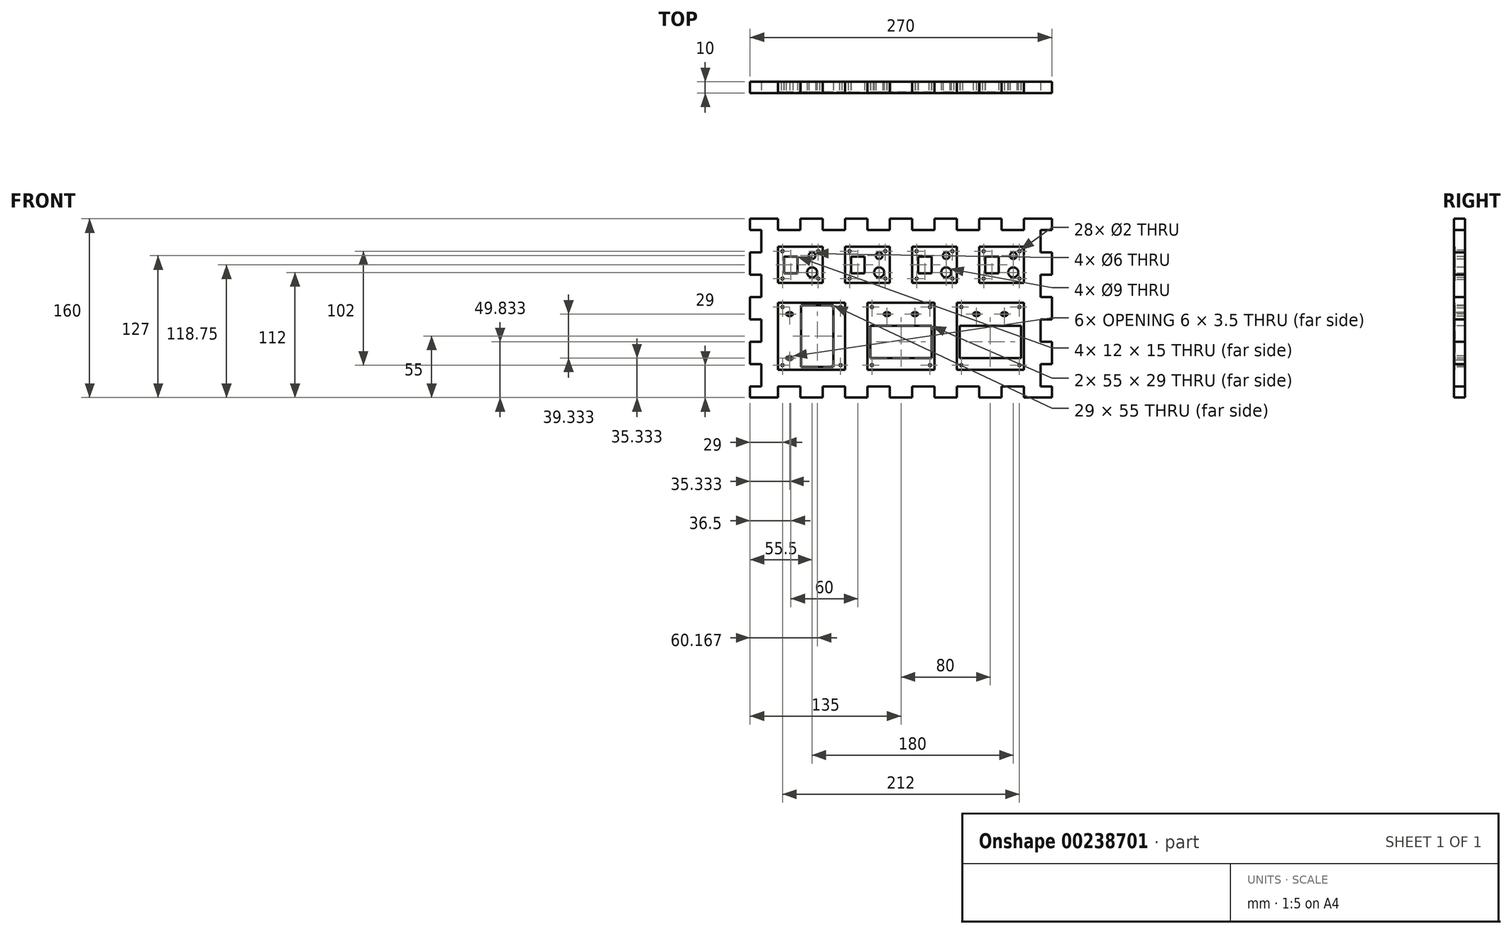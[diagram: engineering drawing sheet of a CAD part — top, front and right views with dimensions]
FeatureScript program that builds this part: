
annotation { "Feature Type Name" : "Feature", "Feature Type Description" : "" }
export const myFeature = defineFeature(function(context is Context, id is Id, definition is map)
    precondition{}
    {
        {
            var Q0;
            Q0=qCreatedBy(makeId("Front.planeOp"),FACE);
            var sketch = newSketch(context, id + "F0", { "sketchPlane" : qUnion([Q0])});
            skCircle(sketch, "E0", {"center": v(26.5, 16.25) * mm, "radius": 6.5 * mm, "construction": true});
            skCircle(sketch, "E1", {"center": v(45.5, 9.5) * mm, "radius": 4.5 * mm});
            skCircle(sketch, "E2", {"center": v(45.5, 9.5) * mm, "radius": 3 * mm});
            skCircle(sketch, "E3", {"center": v(45.5, 24.5) * mm, "radius": 3 * mm});
            skCircle(sketch, "E4", {"center": v(45.5, 24.5) * mm, "radius": 2.5 * mm});
            skLineSegment(sketch, "E5", {"start": v(45.5, 27.5) * mm, "end": v(45.5, 5) * mm, "construction": true});
            skPoint(sketch, "E6.positionSnap0", {"position": v(45.5, 16.25) * mm});
            skLineSegment(sketch, "E7.bottom", {"start": v(15, 32.5) * mm, "end": v(55, 32.5) * mm});
            skLineSegment(sketch, "E7.top", {"start": v(15, 0) * mm, "end": v(55, 0) * mm});
            skLineSegment(sketch, "E7.left", {"start": v(15, 32.5) * mm, "end": v(15, 0) * mm});
            skLineSegment(sketch, "E7.right", {"start": v(55, 32.5) * mm, "end": v(55, 0) * mm});
            skLineSegment(sketch, "E8", {"start": v(20.5, 22.25) * mm, "end": v(20.5, 23.75) * mm});
            skLineSegment(sketch, "E9", {"start": v(20.5, 23.75) * mm, "end": v(32.5, 23.75) * mm});
            skLineSegment(sketch, "E10", {"start": v(32.5, 23.75) * mm, "end": v(32.5, 22.25) * mm});
            skLineSegment(sketch, "E11", {"start": v(15, 16.25) * mm, "end": v(55, 16.25) * mm, "construction": true});
            skLineSegment(sketch, "E12.MirrorCS", {"start": v(32.5, 8.75) * mm, "end": v(32.5, 10.25) * mm});
            skLineSegment(sketch, "E13.MirrorCS", {"start": v(20.5, 8.75) * mm, "end": v(32.5, 8.75) * mm});
            skLineSegment(sketch, "E14.MirrorCS", {"start": v(20.5, 10.25) * mm, "end": v(20.5, 8.75) * mm});
            skLineSegment(sketch, "E15", {"start": v(50, 9.5) * mm, "end": v(55, 9.5) * mm, "construction": true});
            skLineSegment(sketch, "E16", {"start": v(41, 9.5) * mm, "end": v(41, 16.25) * mm, "construction": true});
            skLineSegment(sketch, "E17.bottom", {"start": v(32.5, 22.25) * mm, "end": v(20.5, 22.25) * mm});
            skLineSegment(sketch, "E17.top", {"start": v(32.5, 10.25) * mm, "end": v(20.5, 10.25) * mm});
            skLineSegment(sketch, "E17.left", {"start": v(32.5, 22.25) * mm, "end": v(32.5, 10.25) * mm});
            skLineSegment(sketch, "E17.right", {"start": v(20.5, 22.25) * mm, "end": v(20.5, 10.25) * mm});
            skLineSegment(sketch, "E18.bottom", {"start": v(24.5, 18.25) * mm, "end": v(28.5, 18.25) * mm});
            skLineSegment(sketch, "E18.top", {"start": v(24.5, 14.25) * mm, "end": v(28.5, 14.25) * mm});
            skLineSegment(sketch, "E18.left", {"start": v(24.5, 18.25) * mm, "end": v(24.5, 14.25) * mm});
            skLineSegment(sketch, "E18.right", {"start": v(28.5, 18.25) * mm, "end": v(28.5, 14.25) * mm});
            skLineSegment(sketch, "E19.1.0.0", {"start": v(92.5, 22.25) * mm, "end": v(80.5, 22.25) * mm});
            skCircle(sketch, "E19.1.0.1", {"center": v(105.5, 24.5) * mm, "radius": 2.5 * mm});
            skCircle(sketch, "E19.1.0.3", {"center": v(86.5, 16.25) * mm, "radius": 6.5 * mm, "construction": true});
            skLineSegment(sketch, "E19.1.0.4", {"start": v(115, 32.5) * mm, "end": v(115, 0) * mm});
            skLineSegment(sketch, "E19.1.0.5", {"start": v(75, 32.5) * mm, "end": v(115, 32.5) * mm});
            skLineSegment(sketch, "E19.1.0.6", {"start": v(84.5, 18.25) * mm, "end": v(84.5, 14.25) * mm});
            skLineSegment(sketch, "E19.1.0.7", {"start": v(84.5, 18.25) * mm, "end": v(88.5, 18.25) * mm});
            skLineSegment(sketch, "E19.1.0.8", {"start": v(92.5, 10.25) * mm, "end": v(80.5, 10.25) * mm});
            skLineSegment(sketch, "E19.1.0.9", {"start": v(80.5, 23.75) * mm, "end": v(92.5, 23.75) * mm});
            skCircle(sketch, "E19.1.0.10", {"center": v(105.5, 9.5) * mm, "radius": 4.5 * mm});
            skLineSegment(sketch, "E19.1.0.11", {"start": v(88.5, 18.25) * mm, "end": v(88.5, 14.25) * mm});
            skPoint(sketch, "E19.1.0.13", {"position": v(86.5, 16.25) * mm});
            skLineSegment(sketch, "E19.1.0.14", {"start": v(75, 32.5) * mm, "end": v(75, 0) * mm});
            skLineSegment(sketch, "E19.1.0.15", {"start": v(80.5, 8.75) * mm, "end": v(92.5, 8.75) * mm});
            skCircle(sketch, "E19.1.0.16", {"center": v(105.5, 9.5) * mm, "radius": 3 * mm});
            skCircle(sketch, "E19.1.0.17", {"center": v(105.5, 24.5) * mm, "radius": 3 * mm});
            skLineSegment(sketch, "E19.1.0.18", {"start": v(80.5, 22.25) * mm, "end": v(80.5, 10.25) * mm});
            skLineSegment(sketch, "E19.1.0.19", {"start": v(92.5, 22.25) * mm, "end": v(92.5, 10.25) * mm});
            skLineSegment(sketch, "E19.1.0.20", {"start": v(75, 0) * mm, "end": v(115, 0) * mm});
            skLineSegment(sketch, "E19.1.0.22", {"start": v(84.5, 14.25) * mm, "end": v(88.5, 14.25) * mm});
            skPoint(sketch, "E19.1.0.23", {"position": v(86.5, 16.25) * mm});
            skLineSegment(sketch, "E19.1.0.24", {"start": v(92.5, 23.75) * mm, "end": v(92.5, 22.25) * mm});
            skLineSegment(sketch, "E19.1.0.25", {"start": v(80.5, 22.25) * mm, "end": v(80.5, 23.75) * mm});
            skLineSegment(sketch, "E19.1.0.26", {"start": v(80.5, 10.25) * mm, "end": v(80.5, 8.75) * mm});
            skLineSegment(sketch, "E19.1.0.27", {"start": v(92.5, 8.75) * mm, "end": v(92.5, 10.25) * mm});
            skLineSegment(sketch, "E19.2.0.0", {"start": v(152.5, 22.25) * mm, "end": v(140.5, 22.25) * mm});
            skCircle(sketch, "E19.2.0.1", {"center": v(165.5, 24.5) * mm, "radius": 2.5 * mm});
            skCircle(sketch, "E19.2.0.3", {"center": v(146.5, 16.25) * mm, "radius": 6.5 * mm, "construction": true});
            skLineSegment(sketch, "E19.2.0.4", {"start": v(175, 32.5) * mm, "end": v(175, 0) * mm});
            skLineSegment(sketch, "E19.2.0.5", {"start": v(135, 32.5) * mm, "end": v(175, 32.5) * mm});
            skLineSegment(sketch, "E19.2.0.6", {"start": v(144.5, 18.25) * mm, "end": v(144.5, 14.25) * mm});
            skLineSegment(sketch, "E19.2.0.7", {"start": v(144.5, 18.25) * mm, "end": v(148.5, 18.25) * mm});
            skLineSegment(sketch, "E19.2.0.8", {"start": v(152.5, 10.25) * mm, "end": v(140.5, 10.25) * mm});
            skLineSegment(sketch, "E19.2.0.9", {"start": v(140.5, 23.75) * mm, "end": v(152.5, 23.75) * mm});
            skCircle(sketch, "E19.2.0.10", {"center": v(165.5, 9.5) * mm, "radius": 4.5 * mm});
            skLineSegment(sketch, "E19.2.0.11", {"start": v(148.5, 18.25) * mm, "end": v(148.5, 14.25) * mm});
            skPoint(sketch, "E19.2.0.13", {"position": v(146.5, 16.25) * mm});
            skLineSegment(sketch, "E19.2.0.14", {"start": v(135, 32.5) * mm, "end": v(135, 0) * mm});
            skLineSegment(sketch, "E19.2.0.15", {"start": v(140.5, 8.75) * mm, "end": v(152.5, 8.75) * mm});
            skCircle(sketch, "E19.2.0.16", {"center": v(165.5, 9.5) * mm, "radius": 3 * mm});
            skCircle(sketch, "E19.2.0.17", {"center": v(165.5, 24.5) * mm, "radius": 3 * mm});
            skLineSegment(sketch, "E19.2.0.18", {"start": v(140.5, 22.25) * mm, "end": v(140.5, 10.25) * mm});
            skLineSegment(sketch, "E19.2.0.19", {"start": v(152.5, 22.25) * mm, "end": v(152.5, 10.25) * mm});
            skLineSegment(sketch, "E19.2.0.20", {"start": v(135, 0) * mm, "end": v(175, 0) * mm});
            skLineSegment(sketch, "E19.2.0.22", {"start": v(144.5, 14.25) * mm, "end": v(148.5, 14.25) * mm});
            skPoint(sketch, "E19.2.0.23", {"position": v(146.5, 16.25) * mm});
            skLineSegment(sketch, "E19.2.0.24", {"start": v(152.5, 23.75) * mm, "end": v(152.5, 22.25) * mm});
            skLineSegment(sketch, "E19.2.0.25", {"start": v(140.5, 22.25) * mm, "end": v(140.5, 23.75) * mm});
            skLineSegment(sketch, "E19.2.0.26", {"start": v(140.5, 10.25) * mm, "end": v(140.5, 8.75) * mm});
            skLineSegment(sketch, "E19.2.0.27", {"start": v(152.5, 8.75) * mm, "end": v(152.5, 10.25) * mm});
            skLineSegment(sketch, "E19.3.0.0", {"start": v(212.5, 22.25) * mm, "end": v(200.5, 22.25) * mm});
            skCircle(sketch, "E19.3.0.1", {"center": v(225.5, 24.5) * mm, "radius": 2.5 * mm});
            skCircle(sketch, "E19.3.0.3", {"center": v(206.5, 16.25) * mm, "radius": 6.5 * mm, "construction": true});
            skLineSegment(sketch, "E19.3.0.4", {"start": v(235, 32.5) * mm, "end": v(235, 0) * mm});
            skLineSegment(sketch, "E19.3.0.5", {"start": v(195, 32.5) * mm, "end": v(235, 32.5) * mm});
            skLineSegment(sketch, "E19.3.0.6", {"start": v(204.5, 18.25) * mm, "end": v(204.5, 14.25) * mm});
            skLineSegment(sketch, "E19.3.0.7", {"start": v(204.5, 18.25) * mm, "end": v(208.5, 18.25) * mm});
            skLineSegment(sketch, "E19.3.0.8", {"start": v(212.5, 10.25) * mm, "end": v(200.5, 10.25) * mm});
            skLineSegment(sketch, "E19.3.0.9", {"start": v(200.5, 23.75) * mm, "end": v(212.5, 23.75) * mm});
            skCircle(sketch, "E19.3.0.10", {"center": v(225.5, 9.5) * mm, "radius": 4.5 * mm});
            skLineSegment(sketch, "E19.3.0.11", {"start": v(208.5, 18.25) * mm, "end": v(208.5, 14.25) * mm});
            skPoint(sketch, "E19.3.0.13", {"position": v(206.5, 16.25) * mm});
            skLineSegment(sketch, "E19.3.0.14", {"start": v(195, 32.5) * mm, "end": v(195, 0) * mm});
            skLineSegment(sketch, "E19.3.0.15", {"start": v(200.5, 8.75) * mm, "end": v(212.5, 8.75) * mm});
            skCircle(sketch, "E19.3.0.16", {"center": v(225.5, 9.5) * mm, "radius": 3 * mm});
            skCircle(sketch, "E19.3.0.17", {"center": v(225.5, 24.5) * mm, "radius": 3 * mm});
            skLineSegment(sketch, "E19.3.0.18", {"start": v(200.5, 22.25) * mm, "end": v(200.5, 10.25) * mm});
            skLineSegment(sketch, "E19.3.0.19", {"start": v(212.5, 22.25) * mm, "end": v(212.5, 10.25) * mm});
            skLineSegment(sketch, "E19.3.0.20", {"start": v(195, 0) * mm, "end": v(235, 0) * mm});
            skLineSegment(sketch, "E19.3.0.22", {"start": v(204.5, 14.25) * mm, "end": v(208.5, 14.25) * mm});
            skPoint(sketch, "E19.3.0.23", {"position": v(206.5, 16.25) * mm});
            skLineSegment(sketch, "E19.3.0.24", {"start": v(212.5, 23.75) * mm, "end": v(212.5, 22.25) * mm});
            skLineSegment(sketch, "E19.3.0.25", {"start": v(200.5, 22.25) * mm, "end": v(200.5, 23.75) * mm});
            skLineSegment(sketch, "E19.3.0.26", {"start": v(200.5, 10.25) * mm, "end": v(200.5, 8.75) * mm});
            skLineSegment(sketch, "E19.3.0.27", {"start": v(212.5, 8.75) * mm, "end": v(212.5, 10.25) * mm});
            skLineSegment(sketch, "E19.direction1", {"start": v(15, 0) * mm, "end": v(75, 0) * mm, "construction": true});
            skLineSegment(sketch, "E20.bottom", {"start": v(0, -92.5) * mm, "end": v(250, -92.5) * mm, "construction": true});
            skLineSegment(sketch, "E20.top", {"start": v(0, 47.5) * mm, "end": v(250, 47.5) * mm, "construction": true});
            skLineSegment(sketch, "E20.right", {"start": v(250, -92.5) * mm, "end": v(250, 47.5) * mm, "construction": true});
            skLineSegment(sketch, "E21", {"start": v(115, 0) * mm, "end": v(135, 0) * mm, "construction": true});
            skLineSegment(sketch, "E22.bottom", {"start": v(144.5, -39.17) * mm, "end": v(98.5, -39.17) * mm});
            skLineSegment(sketch, "E22.top", {"start": v(144.5, -66.17) * mm, "end": v(98.5, -66.17) * mm});
            skLineSegment(sketch, "E22.right", {"start": v(98.5, -39.17) * mm, "end": v(98.5, -66.17) * mm});
            skLineSegment(sketch, "E23.bottom", {"start": v(151.5, -39.17) * mm, "end": v(145.5, -39.17) * mm});
            skLineSegment(sketch, "E23.top", {"start": v(151.5, -66.17) * mm, "end": v(145.5, -66.17) * mm});
            skLineSegment(sketch, "E23.left", {"start": v(151.5, -39.17) * mm, "end": v(151.5, -66.17) * mm});
            skLineSegment(sketch, "E24.bottom", {"start": v(152.5, -67.17) * mm, "end": v(97.5, -67.17) * mm});
            skLineSegment(sketch, "E24.top", {"start": v(152.5, -38.17) * mm, "end": v(97.5, -38.17) * mm});
            skLineSegment(sketch, "E24.left", {"start": v(152.5, -67.17) * mm, "end": v(152.5, -38.17) * mm});
            skLineSegment(sketch, "E24.right", {"start": v(97.5, -67.17) * mm, "end": v(97.5, -38.17) * mm});
            skLineSegment(sketch, "E25", {"start": v(145.5, -64.17) * mm, "end": v(144.5, -64.17) * mm});
            skLineSegment(sketch, "E26", {"start": v(145.5, -41.17) * mm, "end": v(144.5, -41.17) * mm});
            skLineSegment(sketch, "E27", {"start": v(145.5, -66.17) * mm, "end": v(145.5, -64.17) * mm});
            skLineSegment(sketch, "E28", {"start": v(144.5, -66.17) * mm, "end": v(144.5, -64.17) * mm});
            skLineSegment(sketch, "E29", {"start": v(145.5, -41.17) * mm, "end": v(145.5, -39.17) * mm});
            skLineSegment(sketch, "E30", {"start": v(144.5, -41.17) * mm, "end": v(144.5, -39.17) * mm});
            skLineSegment(sketch, "E31.bottom", {"start": v(95, -77.5) * mm, "end": v(95, -17.5) * mm});
            skLineSegment(sketch, "E31.top", {"start": v(155, -77.5) * mm, "end": v(155, -17.5) * mm});
            skLineSegment(sketch, "E31.left", {"start": v(95, -77.5) * mm, "end": v(155, -77.5) * mm});
            skLineSegment(sketch, "E31.right", {"start": v(95, -17.5) * mm, "end": v(155, -17.5) * mm});
            skLineSegment(sketch, "E32", {"start": v(125, -38.17) * mm, "end": v(125, -17.5) * mm, "construction": true});
            skLineSegment(sketch, "E33", {"start": v(97.5, -67.17) * mm, "end": v(97.5, -77.5) * mm, "construction": true});
            skLineSegment(sketch, "E34", {"start": v(125, 0) * mm, "end": v(125, -92.5) * mm, "construction": true});
            skLineSegment(sketch, "E35.1.0.0", {"start": v(175, -77.5) * mm, "end": v(175, -17.5) * mm});
            skLineSegment(sketch, "E35.1.0.1", {"start": v(235, -77.5) * mm, "end": v(235, -17.5) * mm});
            skLineSegment(sketch, "E35.1.0.2", {"start": v(232.5, -67.17) * mm, "end": v(177.5, -67.17) * mm});
            skLineSegment(sketch, "E35.1.0.3", {"start": v(232.5, -67.17) * mm, "end": v(232.5, -38.17) * mm});
            skLineSegment(sketch, "E35.1.0.4", {"start": v(175, -17.5) * mm, "end": v(235, -17.5) * mm});
            skLineSegment(sketch, "E35.1.0.5", {"start": v(178.5, -39.17) * mm, "end": v(178.5, -66.17) * mm});
            skLineSegment(sketch, "E35.1.0.9", {"start": v(224.5, -66.17) * mm, "end": v(178.5, -66.17) * mm});
            skLineSegment(sketch, "E35.1.0.10", {"start": v(205, -38.17) * mm, "end": v(205, -17.5) * mm, "construction": true});
            skLineSegment(sketch, "E35.1.0.11", {"start": v(177.5, -67.17) * mm, "end": v(177.5, -77.5) * mm, "construction": true});
            skLineSegment(sketch, "E35.1.0.12", {"start": v(232.5, -38.17) * mm, "end": v(177.5, -38.17) * mm});
            skLineSegment(sketch, "E35.1.0.14", {"start": v(224.5, -39.17) * mm, "end": v(178.5, -39.17) * mm});
            skLineSegment(sketch, "E35.1.0.17", {"start": v(175, -77.5) * mm, "end": v(235, -77.5) * mm});
            skLineSegment(sketch, "E35.1.0.18", {"start": v(231.5, -39.17) * mm, "end": v(231.5, -66.17) * mm});
            skLineSegment(sketch, "E35.1.0.19", {"start": v(177.5, -67.17) * mm, "end": v(177.5, -38.17) * mm});
            skLineSegment(sketch, "E35.1.0.23", {"start": v(224.5, -41.17) * mm, "end": v(224.5, -39.17) * mm});
            skLineSegment(sketch, "E35.1.0.24", {"start": v(231.5, -39.17) * mm, "end": v(225.5, -39.17) * mm});
            skLineSegment(sketch, "E35.1.0.25", {"start": v(225.5, -41.17) * mm, "end": v(225.5, -39.17) * mm});
            skLineSegment(sketch, "E35.1.0.26", {"start": v(231.5, -66.17) * mm, "end": v(225.5, -66.17) * mm});
            skLineSegment(sketch, "E35.1.0.27", {"start": v(225.5, -66.17) * mm, "end": v(225.5, -64.17) * mm});
            skLineSegment(sketch, "E35.1.0.28", {"start": v(225.5, -41.17) * mm, "end": v(224.5, -41.17) * mm});
            skLineSegment(sketch, "E35.1.0.29", {"start": v(224.5, -66.17) * mm, "end": v(224.5, -64.17) * mm});
            skLineSegment(sketch, "E35.1.0.30", {"start": v(225.5, -64.17) * mm, "end": v(224.5, -64.17) * mm});
            skLineSegment(sketch, "E35.direction1", {"start": v(95, -77.5) * mm, "end": v(175, -77.5) * mm, "construction": true});
            skLineSegment(sketch, "E36.bottom", {"start": v(36.67, -28) * mm, "end": v(36.67, -74) * mm});
            skLineSegment(sketch, "E36.top", {"start": v(63.67, -28) * mm, "end": v(63.67, -74) * mm});
            skLineSegment(sketch, "E36.right", {"start": v(36.67, -74) * mm, "end": v(63.67, -74) * mm});
            skLineSegment(sketch, "E37.bottom", {"start": v(36.67, -21) * mm, "end": v(36.67, -27) * mm});
            skLineSegment(sketch, "E37.top", {"start": v(63.67, -21) * mm, "end": v(63.67, -27) * mm});
            skLineSegment(sketch, "E37.left", {"start": v(36.67, -21) * mm, "end": v(63.67, -21) * mm});
            skLineSegment(sketch, "E38.bottom", {"start": v(64.67, -20) * mm, "end": v(64.67, -75) * mm});
            skLineSegment(sketch, "E38.top", {"start": v(35.67, -20) * mm, "end": v(35.67, -75) * mm});
            skLineSegment(sketch, "E38.left", {"start": v(64.67, -20) * mm, "end": v(35.67, -20) * mm});
            skLineSegment(sketch, "E38.right", {"start": v(64.67, -75) * mm, "end": v(35.67, -75) * mm});
            skLineSegment(sketch, "E39", {"start": v(61.67, -27) * mm, "end": v(61.67, -28) * mm});
            skLineSegment(sketch, "E40", {"start": v(38.67, -27) * mm, "end": v(38.67, -28) * mm});
            skLineSegment(sketch, "E41", {"start": v(63.67, -27) * mm, "end": v(61.67, -27) * mm});
            skLineSegment(sketch, "E42", {"start": v(63.67, -28) * mm, "end": v(61.67, -28) * mm});
            skLineSegment(sketch, "E43", {"start": v(38.67, -27) * mm, "end": v(36.67, -27) * mm});
            skLineSegment(sketch, "E44", {"start": v(38.67, -28) * mm, "end": v(36.67, -28) * mm});
            skLineSegment(sketch, "E45.bottom", {"start": v(75, -77.5) * mm, "end": v(15, -77.5) * mm});
            skLineSegment(sketch, "E45.top", {"start": v(75, -17.5) * mm, "end": v(15, -17.5) * mm});
            skLineSegment(sketch, "E45.left", {"start": v(75, -77.5) * mm, "end": v(75, -17.5) * mm});
            skLineSegment(sketch, "E45.right", {"start": v(15, -77.5) * mm, "end": v(15, -17.5) * mm});
            skLineSegment(sketch, "E46", {"start": v(25.33, -29.08) * mm, "end": v(15, -29.08) * mm, "construction": true});
            skLineSegment(sketch, "E47", {"start": v(64.67, -29.08) * mm, "end": v(75, -29.08) * mm, "construction": true});
            skLineSegment(sketch, "E48", {"start": v(25.33, -29.08) * mm, "end": v(35.67, -29.08) * mm, "construction": true});
            skCircle(sketch, "E49", {"center": v(19, 28.5) * mm, "radius": 1 * mm});
            skCircle(sketch, "E50", {"center": v(51, 28.5) * mm, "radius": 1 * mm});
            skCircle(sketch, "E51", {"center": v(51, 4) * mm, "radius": 1 * mm});
            skCircle(sketch, "E52", {"center": v(19, 4) * mm, "radius": 1 * mm});
            skCircle(sketch, "E53", {"center": v(19, -21.5) * mm, "radius": 1 * mm});
            skCircle(sketch, "E54", {"center": v(71, -21.5) * mm, "radius": 1 * mm});
            skCircle(sketch, "E55", {"center": v(19, -73.5) * mm, "radius": 1 * mm});
            skCircle(sketch, "E56", {"center": v(71, -73.5) * mm, "radius": 1 * mm});
            skCircle(sketch, "E57.1.0.0", {"center": v(79, 28.5) * mm, "radius": 1 * mm});
            skCircle(sketch, "E57.1.0.1", {"center": v(79, 4) * mm, "radius": 1 * mm});
            skCircle(sketch, "E57.1.0.2", {"center": v(111, 4) * mm, "radius": 1 * mm});
            skCircle(sketch, "E57.1.0.3", {"center": v(111, 28.5) * mm, "radius": 1 * mm});
            skCircle(sketch, "E57.2.0.0", {"center": v(139, 28.5) * mm, "radius": 1 * mm});
            skCircle(sketch, "E57.2.0.1", {"center": v(139, 4) * mm, "radius": 1 * mm});
            skCircle(sketch, "E57.2.0.2", {"center": v(171, 4) * mm, "radius": 1 * mm});
            skCircle(sketch, "E57.2.0.3", {"center": v(171, 28.5) * mm, "radius": 1 * mm});
            skCircle(sketch, "E57.3.0.0", {"center": v(199, 28.5) * mm, "radius": 1 * mm});
            skCircle(sketch, "E57.3.0.1", {"center": v(199, 4) * mm, "radius": 1 * mm});
            skCircle(sketch, "E57.3.0.2", {"center": v(231, 4) * mm, "radius": 1 * mm});
            skCircle(sketch, "E57.3.0.3", {"center": v(231, 28.5) * mm, "radius": 1 * mm});
            skLineSegment(sketch, "E57.direction1", {"start": v(19, 4) * mm, "end": v(79, 4) * mm, "construction": true});
            skCircle(sketch, "E58.1.0.0", {"center": v(99, -73.5) * mm, "radius": 1 * mm});
            skCircle(sketch, "E58.1.0.1", {"center": v(151, -73.5) * mm, "radius": 1 * mm});
            skCircle(sketch, "E58.1.0.2", {"center": v(151, -21.5) * mm, "radius": 1 * mm});
            skCircle(sketch, "E58.1.0.3", {"center": v(99, -21.5) * mm, "radius": 1 * mm});
            skCircle(sketch, "E58.2.0.0", {"center": v(179, -73.5) * mm, "radius": 1 * mm});
            skCircle(sketch, "E58.2.0.1", {"center": v(231, -73.5) * mm, "radius": 1 * mm});
            skCircle(sketch, "E58.2.0.2", {"center": v(231, -21.5) * mm, "radius": 1 * mm});
            skCircle(sketch, "E58.2.0.3", {"center": v(179, -21.5) * mm, "radius": 1 * mm});
            skLineSegment(sketch, "E58.direction1", {"start": v(19, -73.5) * mm, "end": v(99, -73.5) * mm, "construction": true});
            skPoint(sketch, "E59.middle", {"position": v(25.33, -27.83) * mm});
            skLineSegment(sketch, "E60", {"start": v(15, -47.5) * mm, "end": v(35.67, -47.5) * mm, "construction": true});
            skPoint(sketch, "E61.1.0.0", {"position": v(112.5, -27.83) * mm});
            skLineSegment(sketch, "E62", {"start": v(112.5, -26.58) * mm, "end": v(112.5, -27.83) * mm, "construction": true});
            skLineSegment(sketch, "E63.bottom", {"start": v(115, -29.08) * mm, "end": v(110, -29.08) * mm, "construction": true});
            skLineSegment(sketch, "E63.top", {"start": v(115, -26.58) * mm, "end": v(110, -26.58) * mm, "construction": true});
            skLineSegment(sketch, "E63.left", {"start": v(115, -29.08) * mm, "end": v(115, -26.58) * mm, "construction": true});
            skLineSegment(sketch, "E63.right", {"start": v(110, -29.08) * mm, "end": v(110, -26.58) * mm, "construction": true});
            skFitSpline(sketch, "E64", {"points": [v(110, -27.83) * mm, v(110.5, -27.13) * mm, v(112.5, -26.58) * mm], "startDerivative": vector(0, 1.91) * mm, "endDerivative": vector(3.95, 0) * mm});
            skLineSegment(sketch, "E65", {"start": v(110, -27.83) * mm, "end": v(112.5, -27.83) * mm, "construction": true});
            skFitSpline(sketch, "E66.MirrorCS", {"points": [v(115, -27.83) * mm, v(114.5, -27.13) * mm, v(112.5, -26.58) * mm], "startDerivative": vector(0, 1.91) * mm, "endDerivative": vector(-3.95, 0) * mm});
            skFitSpline(sketch, "E67.MirrorCS", {"points": [v(110, -27.83) * mm, v(110.5, -28.53) * mm, v(112.5, -29.08) * mm], "startDerivative": vector(0, -1.91) * mm, "endDerivative": vector(3.95, 0) * mm});
            skFitSpline(sketch, "E68.MirrorCS", {"points": [v(115, -27.83) * mm, v(114.5, -28.53) * mm, v(112.5, -29.08) * mm], "startDerivative": vector(0, -1.91) * mm, "endDerivative": vector(-3.95, 0) * mm});
            skLineSegment(sketch, "E69", {"start": v(25.33, -17.5) * mm, "end": v(25.33, -27.83) * mm, "construction": true});
            skLineSegment(sketch, "E70.bottom", {"start": v(27.83, -29.08) * mm, "end": v(22.83, -29.08) * mm, "construction": true});
            skLineSegment(sketch, "E70.top", {"start": v(27.83, -26.58) * mm, "end": v(22.83, -26.58) * mm, "construction": true});
            skLineSegment(sketch, "E70.left", {"start": v(27.83, -29.08) * mm, "end": v(27.83, -26.58) * mm, "construction": true});
            skLineSegment(sketch, "E70.right", {"start": v(22.83, -29.08) * mm, "end": v(22.83, -26.58) * mm, "construction": true});
            skFitSpline(sketch, "E71", {"points": [v(22.83, -27.83) * mm, v(23.33, -27.13) * mm, v(25.33, -26.58) * mm], "startDerivative": vector(0, 1.91) * mm, "endDerivative": vector(3.95, 0) * mm});
            skLineSegment(sketch, "E72", {"start": v(22.83, -27.83) * mm, "end": v(25.33, -27.83) * mm, "construction": true});
            skFitSpline(sketch, "E73.MirrorCS", {"points": [v(27.83, -27.83) * mm, v(27.33, -27.13) * mm, v(25.33, -26.58) * mm], "startDerivative": vector(0, 1.91) * mm, "endDerivative": vector(-3.95, 0) * mm});
            skFitSpline(sketch, "E74.MirrorCS", {"points": [v(22.83, -27.83) * mm, v(23.33, -28.53) * mm, v(25.33, -29.08) * mm], "startDerivative": vector(0, -1.91) * mm, "endDerivative": vector(3.95, 0) * mm});
            skFitSpline(sketch, "E75.MirrorCS", {"points": [v(27.83, -27.83) * mm, v(27.33, -28.53) * mm, v(25.33, -29.08) * mm], "startDerivative": vector(0, -1.91) * mm, "endDerivative": vector(-3.95, 0) * mm});
            skFitSpline(sketch, "E76.MirrorCS", {"points": [v(135, -27.83) * mm, v(135.5, -27.13) * mm, v(137.5, -26.58) * mm], "startDerivative": vector(0, 1.91) * mm, "endDerivative": vector(3.95, 0) * mm});
            skFitSpline(sketch, "E77.MirrorCS", {"points": [v(135, -27.83) * mm, v(135.5, -28.53) * mm, v(137.5, -29.08) * mm], "startDerivative": vector(0, -1.91) * mm, "endDerivative": vector(3.95, 0) * mm});
            skFitSpline(sketch, "E78.MirrorCS", {"points": [v(140, -27.83) * mm, v(139.5, -28.53) * mm, v(137.5, -29.08) * mm], "startDerivative": vector(0, -1.91) * mm, "endDerivative": vector(-3.95, 0) * mm});
            skFitSpline(sketch, "E79.MirrorCS", {"points": [v(140, -27.83) * mm, v(139.5, -27.13) * mm, v(137.5, -26.58) * mm], "startDerivative": vector(0, 1.91) * mm, "endDerivative": vector(-3.95, 0) * mm});
            skPoint(sketch, "E80.MirrorP", {"position": v(137.5, -27.83) * mm});
            skFitSpline(sketch, "E81.MirrorCS", {"points": [v(27.83, -67.17) * mm, v(27.33, -66.47) * mm, v(25.33, -65.92) * mm], "startDerivative": vector(0, 1.91) * mm, "endDerivative": vector(-3.95, 0) * mm});
            skFitSpline(sketch, "E82.MirrorCS", {"points": [v(27.83, -67.17) * mm, v(27.33, -67.87) * mm, v(25.33, -68.42) * mm], "startDerivative": vector(0, -1.91) * mm, "endDerivative": vector(-3.95, 0) * mm});
            skFitSpline(sketch, "E83.MirrorCS", {"points": [v(22.83, -67.17) * mm, v(23.33, -67.87) * mm, v(25.33, -68.42) * mm], "startDerivative": vector(0, -1.91) * mm, "endDerivative": vector(3.95, 0) * mm});
            skFitSpline(sketch, "E84.MirrorCS", {"points": [v(22.83, -67.17) * mm, v(23.33, -66.47) * mm, v(25.33, -65.92) * mm], "startDerivative": vector(0, 1.91) * mm, "endDerivative": vector(3.95, 0) * mm});
            skPoint(sketch, "E85.1.0.0", {"position": v(192.5, -27.83) * mm});
            skLineSegment(sketch, "E86", {"start": v(192.5, -26.58) * mm, "end": v(192.5, -27.83) * mm, "construction": true});
            skLineSegment(sketch, "E87.bottom", {"start": v(195, -29.08) * mm, "end": v(190, -29.08) * mm, "construction": true});
            skLineSegment(sketch, "E87.top", {"start": v(195, -26.58) * mm, "end": v(190, -26.58) * mm, "construction": true});
            skLineSegment(sketch, "E87.left", {"start": v(195, -29.08) * mm, "end": v(195, -26.58) * mm, "construction": true});
            skLineSegment(sketch, "E87.right", {"start": v(190, -29.08) * mm, "end": v(190, -26.58) * mm, "construction": true});
            skFitSpline(sketch, "E88", {"points": [v(190, -27.83) * mm, v(190.5, -27.13) * mm, v(192.5, -26.58) * mm], "startDerivative": vector(0, 1.91) * mm, "endDerivative": vector(3.95, 0) * mm});
            skLineSegment(sketch, "E89", {"start": v(190, -27.83) * mm, "end": v(192.5, -27.83) * mm, "construction": true});
            skFitSpline(sketch, "E90.MirrorCS", {"points": [v(195, -27.83) * mm, v(194.5, -27.13) * mm, v(192.5, -26.58) * mm], "startDerivative": vector(0, 1.91) * mm, "endDerivative": vector(-3.95, 0) * mm});
            skFitSpline(sketch, "E91.MirrorCS", {"points": [v(190, -27.83) * mm, v(190.5, -28.53) * mm, v(192.5, -29.08) * mm], "startDerivative": vector(0, -1.91) * mm, "endDerivative": vector(3.95, 0) * mm});
            skFitSpline(sketch, "E92.MirrorCS", {"points": [v(195, -27.83) * mm, v(194.5, -28.53) * mm, v(192.5, -29.08) * mm], "startDerivative": vector(0, -1.91) * mm, "endDerivative": vector(-3.95, 0) * mm});
            skFitSpline(sketch, "E93.MirrorCS", {"points": [v(215, -27.83) * mm, v(215.5, -27.13) * mm, v(217.5, -26.58) * mm], "startDerivative": vector(0, 1.91) * mm, "endDerivative": vector(3.95, 0) * mm});
            skFitSpline(sketch, "E94.MirrorCS", {"points": [v(220, -27.83) * mm, v(219.5, -27.13) * mm, v(217.5, -26.58) * mm], "startDerivative": vector(0, 1.91) * mm, "endDerivative": vector(-3.95, 0) * mm});
            skFitSpline(sketch, "E95.MirrorCS", {"points": [v(220, -27.83) * mm, v(219.5, -28.53) * mm, v(217.5, -29.08) * mm], "startDerivative": vector(0, -1.91) * mm, "endDerivative": vector(-3.95, 0) * mm});
            skFitSpline(sketch, "E96.MirrorCS", {"points": [v(215, -27.83) * mm, v(215.5, -28.53) * mm, v(217.5, -29.08) * mm], "startDerivative": vector(0, -1.91) * mm, "endDerivative": vector(3.95, 0) * mm});
            skPoint(sketch, "E97.MirrorP", {"position": v(217.5, -27.83) * mm});
            skFitSpline(sketch, "E98.0", {"points": [v(28.33, -67.17) * mm, v(28.33, -67.33) * mm, v(28.25, -67.64) * mm, v(28, -67.98) * mm, v(27.67, -68.26) * mm, v(27.3, -68.48) * mm, v(26.86, -68.67) * mm, v(26.23, -68.85) * mm, v(25.7, -68.92) * mm, v(25.33, -68.92) * mm]});
            skFitSpline(sketch, "E98.1", {"points": [v(28.33, -67.17) * mm, v(28.33, -67) * mm, v(28.25, -66.7) * mm, v(28, -66.35) * mm, v(27.67, -66.08) * mm, v(27.3, -65.85) * mm, v(26.86, -65.67) * mm, v(26.23, -65.48) * mm, v(25.7, -65.42) * mm, v(25.33, -65.42) * mm]});
            skFitSpline(sketch, "E98.2", {"points": [v(22.33, -67.17) * mm, v(22.33, -67) * mm, v(22.42, -66.7) * mm, v(22.67, -66.35) * mm, v(23, -66.08) * mm, v(23.37, -65.85) * mm, v(23.8, -65.67) * mm, v(24.43, -65.48) * mm, v(24.97, -65.42) * mm, v(25.33, -65.42) * mm]});
            skFitSpline(sketch, "E98.3", {"points": [v(22.33, -67.17) * mm, v(22.33, -67.33) * mm, v(22.42, -67.64) * mm, v(22.67, -67.98) * mm, v(23, -68.26) * mm, v(23.37, -68.48) * mm, v(23.8, -68.67) * mm, v(24.43, -68.85) * mm, v(24.97, -68.92) * mm, v(25.33, -68.92) * mm]});
            skFitSpline(sketch, "E99.0", {"points": [v(28.33, -27.83) * mm, v(28.33, -28) * mm, v(28.25, -28.3) * mm, v(28, -28.65) * mm, v(27.67, -28.92) * mm, v(27.3, -29.15) * mm, v(26.86, -29.33) * mm, v(26.23, -29.52) * mm, v(25.7, -29.58) * mm, v(25.33, -29.58) * mm]});
            skFitSpline(sketch, "E99.1", {"points": [v(28.33, -27.83) * mm, v(28.33, -27.67) * mm, v(28.25, -27.36) * mm, v(28, -27.02) * mm, v(27.67, -26.74) * mm, v(27.3, -26.52) * mm, v(26.86, -26.33) * mm, v(26.23, -26.15) * mm, v(25.7, -26.08) * mm, v(25.33, -26.08) * mm]});
            skFitSpline(sketch, "E99.2", {"points": [v(22.33, -27.83) * mm, v(22.33, -27.67) * mm, v(22.42, -27.36) * mm, v(22.67, -27.02) * mm, v(23, -26.74) * mm, v(23.37, -26.52) * mm, v(23.8, -26.33) * mm, v(24.43, -26.15) * mm, v(24.97, -26.08) * mm, v(25.33, -26.08) * mm]});
            skFitSpline(sketch, "E99.3", {"points": [v(22.33, -27.83) * mm, v(22.33, -28) * mm, v(22.42, -28.3) * mm, v(22.67, -28.65) * mm, v(23, -28.92) * mm, v(23.37, -29.15) * mm, v(23.8, -29.33) * mm, v(24.43, -29.52) * mm, v(24.97, -29.58) * mm, v(25.33, -29.58) * mm]});
            skFitSpline(sketch, "E100.0", {"points": [v(115.5, -27.83) * mm, v(115.5, -28) * mm, v(115.42, -28.3) * mm, v(115.16, -28.65) * mm, v(114.84, -28.92) * mm, v(114.46, -29.15) * mm, v(114.03, -29.33) * mm, v(113.4, -29.52) * mm, v(112.87, -29.58) * mm, v(112.5, -29.58) * mm]});
            skFitSpline(sketch, "E100.1", {"points": [v(115.5, -27.83) * mm, v(115.5, -27.67) * mm, v(115.42, -27.36) * mm, v(115.16, -27.02) * mm, v(114.84, -26.74) * mm, v(114.46, -26.52) * mm, v(114.03, -26.33) * mm, v(113.4, -26.15) * mm, v(112.87, -26.08) * mm, v(112.5, -26.08) * mm]});
            skFitSpline(sketch, "E100.2", {"points": [v(109.5, -27.83) * mm, v(109.5, -27.67) * mm, v(109.58, -27.36) * mm, v(109.84, -27.02) * mm, v(110.16, -26.74) * mm, v(110.54, -26.52) * mm, v(110.97, -26.33) * mm, v(111.6, -26.15) * mm, v(112.13, -26.08) * mm, v(112.5, -26.08) * mm]});
            skFitSpline(sketch, "E100.3", {"points": [v(109.5, -27.83) * mm, v(109.5, -28) * mm, v(109.58, -28.3) * mm, v(109.84, -28.65) * mm, v(110.16, -28.92) * mm, v(110.54, -29.15) * mm, v(110.97, -29.33) * mm, v(111.6, -29.52) * mm, v(112.13, -29.58) * mm, v(112.5, -29.58) * mm]});
            skFitSpline(sketch, "E101.0", {"points": [v(195.5, -27.83) * mm, v(195.5, -27.67) * mm, v(195.42, -27.36) * mm, v(195.16, -27.02) * mm, v(194.84, -26.74) * mm, v(194.46, -26.52) * mm, v(194.03, -26.33) * mm, v(193.4, -26.15) * mm, v(192.87, -26.08) * mm, v(192.5, -26.08) * mm]});
            skFitSpline(sketch, "E101.1", {"points": [v(195.5, -27.83) * mm, v(195.5, -28) * mm, v(195.42, -28.3) * mm, v(195.16, -28.65) * mm, v(194.84, -28.92) * mm, v(194.46, -29.15) * mm, v(194.03, -29.33) * mm, v(193.4, -29.52) * mm, v(192.87, -29.58) * mm, v(192.5, -29.58) * mm]});
            skFitSpline(sketch, "E101.2", {"points": [v(189.5, -27.83) * mm, v(189.5, -28) * mm, v(189.58, -28.3) * mm, v(189.84, -28.65) * mm, v(190.16, -28.92) * mm, v(190.54, -29.15) * mm, v(190.97, -29.33) * mm, v(191.6, -29.52) * mm, v(192.13, -29.58) * mm, v(192.5, -29.58) * mm]});
            skFitSpline(sketch, "E101.3", {"points": [v(189.5, -27.83) * mm, v(189.5, -27.67) * mm, v(189.58, -27.36) * mm, v(189.84, -27.02) * mm, v(190.16, -26.74) * mm, v(190.54, -26.52) * mm, v(190.97, -26.33) * mm, v(191.6, -26.15) * mm, v(192.13, -26.08) * mm, v(192.5, -26.08) * mm]});
            skFitSpline(sketch, "E102.0", {"points": [v(134.5, -27.83) * mm, v(134.5, -28) * mm, v(134.58, -28.3) * mm, v(134.84, -28.65) * mm, v(135.16, -28.92) * mm, v(135.54, -29.15) * mm, v(135.97, -29.33) * mm, v(136.6, -29.52) * mm, v(137.13, -29.58) * mm, v(137.5, -29.58) * mm]});
            skFitSpline(sketch, "E102.1", {"points": [v(134.5, -27.83) * mm, v(134.5, -27.67) * mm, v(134.58, -27.36) * mm, v(134.84, -27.02) * mm, v(135.16, -26.74) * mm, v(135.54, -26.52) * mm, v(135.97, -26.33) * mm, v(136.6, -26.15) * mm, v(137.13, -26.08) * mm, v(137.5, -26.08) * mm]});
            skFitSpline(sketch, "E102.2", {"points": [v(140.5, -27.83) * mm, v(140.5, -27.67) * mm, v(140.42, -27.36) * mm, v(140.16, -27.02) * mm, v(139.84, -26.74) * mm, v(139.46, -26.52) * mm, v(139.03, -26.33) * mm, v(138.4, -26.15) * mm, v(137.87, -26.08) * mm, v(137.5, -26.08) * mm]});
            skFitSpline(sketch, "E102.3", {"points": [v(140.5, -27.83) * mm, v(140.5, -28) * mm, v(140.42, -28.3) * mm, v(140.16, -28.65) * mm, v(139.84, -28.92) * mm, v(139.46, -29.15) * mm, v(139.03, -29.33) * mm, v(138.4, -29.52) * mm, v(137.87, -29.58) * mm, v(137.5, -29.58) * mm]});
            skFitSpline(sketch, "E103.0", {"points": [v(220.5, -27.83) * mm, v(220.5, -28) * mm, v(220.42, -28.3) * mm, v(220.16, -28.65) * mm, v(219.84, -28.92) * mm, v(219.46, -29.15) * mm, v(219.03, -29.33) * mm, v(218.4, -29.52) * mm, v(217.87, -29.58) * mm, v(217.5, -29.58) * mm]});
            skFitSpline(sketch, "E103.1", {"points": [v(220.5, -27.83) * mm, v(220.5, -27.67) * mm, v(220.42, -27.36) * mm, v(220.16, -27.02) * mm, v(219.84, -26.74) * mm, v(219.46, -26.52) * mm, v(219.03, -26.33) * mm, v(218.4, -26.15) * mm, v(217.87, -26.08) * mm, v(217.5, -26.08) * mm]});
            skFitSpline(sketch, "E103.2", {"points": [v(214.5, -27.83) * mm, v(214.5, -27.67) * mm, v(214.58, -27.36) * mm, v(214.84, -27.02) * mm, v(215.16, -26.74) * mm, v(215.54, -26.52) * mm, v(215.97, -26.33) * mm, v(216.6, -26.15) * mm, v(217.13, -26.08) * mm, v(217.5, -26.08) * mm]});
            skFitSpline(sketch, "E103.3", {"points": [v(214.5, -27.83) * mm, v(214.5, -28) * mm, v(214.58, -28.3) * mm, v(214.84, -28.65) * mm, v(215.16, -28.92) * mm, v(215.54, -29.15) * mm, v(215.97, -29.33) * mm, v(216.6, -29.52) * mm, v(217.13, -29.58) * mm, v(217.5, -29.58) * mm]});
            skLineSegment(sketch, "E104.top", {"start": v(135, -102.5) * mm, "end": v(115, -102.5) * mm});
            skLineSegment(sketch, "E104.left", {"start": v(135, -92.5) * mm, "end": v(135, -102.5) * mm});
            skLineSegment(sketch, "E104.right", {"start": v(115, -92.5) * mm, "end": v(115, -102.5) * mm});
            skPoint(sketch, "E104.middle", {"position": v(125, -97.5) * mm});
            skLineSegment(sketch, "E105", {"start": v(135, -92.5) * mm, "end": v(155, -92.5) * mm});
            skLineSegment(sketch, "E106.1.0.0", {"start": v(155, -92.5) * mm, "end": v(155, -102.5) * mm});
            skLineSegment(sketch, "E106.1.0.1", {"start": v(175, -102.5) * mm, "end": v(155, -102.5) * mm});
            skLineSegment(sketch, "E106.1.0.2", {"start": v(175, -92.5) * mm, "end": v(175, -102.5) * mm});
            skLineSegment(sketch, "E106.1.0.3", {"start": v(175, -92.5) * mm, "end": v(195, -92.5) * mm});
            skLineSegment(sketch, "E106.2.0.0", {"start": v(195, -92.5) * mm, "end": v(195, -102.5) * mm});
            skLineSegment(sketch, "E106.2.0.1", {"start": v(215, -102.5) * mm, "end": v(195, -102.5) * mm});
            skLineSegment(sketch, "E106.2.0.2", {"start": v(215, -92.5) * mm, "end": v(215, -102.5) * mm});
            skLineSegment(sketch, "E106.2.0.3", {"start": v(215, -92.5) * mm, "end": v(235, -92.5) * mm});
            skLineSegment(sketch, "E106.direction1", {"start": v(115, -102.5) * mm, "end": v(155, -102.5) * mm, "construction": true});
            skLineSegment(sketch, "E107.0.3.0", {"start": v(235, -92.5) * mm, "end": v(235, -102.5) * mm});
            skLineSegment(sketch, "E108.MirrorCS", {"start": v(15, -92.5) * mm, "end": v(15, -102.5) * mm});
            skLineSegment(sketch, "E109.MirrorCS", {"start": v(35, -92.5) * mm, "end": v(35, -102.5) * mm});
            skLineSegment(sketch, "E110.MirrorCS", {"start": v(35, -102.5) * mm, "end": v(55, -102.5) * mm});
            skLineSegment(sketch, "E111.MirrorCS", {"start": v(55, -92.5) * mm, "end": v(55, -102.5) * mm});
            skLineSegment(sketch, "E112.MirrorCS", {"start": v(75, -92.5) * mm, "end": v(75, -102.5) * mm});
            skLineSegment(sketch, "E113.MirrorCS", {"start": v(75, -102.5) * mm, "end": v(95, -102.5) * mm});
            skLineSegment(sketch, "E114.MirrorCS", {"start": v(95, -92.5) * mm, "end": v(95, -102.5) * mm});
            skLineSegment(sketch, "E115.MirrorCS", {"start": v(35, -92.5) * mm, "end": v(15, -92.5) * mm});
            skLineSegment(sketch, "E116.MirrorCS", {"start": v(115, -92.5) * mm, "end": v(95, -92.5) * mm});
            skLineSegment(sketch, "E117.MirrorCS", {"start": v(75, -92.5) * mm, "end": v(55, -92.5) * mm});
            skLineSegment(sketch, "E118.bottom", {"start": v(250, -12.5) * mm, "end": v(260, -12.5) * mm});
            skLineSegment(sketch, "E118.top", {"start": v(250, -32.5) * mm, "end": v(260, -32.5) * mm});
            skLineSegment(sketch, "E118.right", {"start": v(260, -12.5) * mm, "end": v(260, -32.5) * mm});
            skPoint(sketch, "E118.middle", {"position": v(255, -22.5) * mm});
            skPoint(sketch, "E118.middle.positionSnap0", {"position": v(250, -22.5) * mm});
            skPoint(sketch, "E118.centerSnap0", {"position": v(250, -22.5) * mm});
            skLineSegment(sketch, "E119", {"start": v(250, -12.5) * mm, "end": v(250, 7.5) * mm});
            skLineSegment(sketch, "E120.0.1.0", {"start": v(250, 7.5) * mm, "end": v(260, 7.5) * mm});
            skLineSegment(sketch, "E120.0.1.1", {"start": v(260, 27.5) * mm, "end": v(260, 7.5) * mm});
            skLineSegment(sketch, "E120.0.1.2", {"start": v(250, 27.5) * mm, "end": v(260, 27.5) * mm});
            skLineSegment(sketch, "E120.0.1.3", {"start": v(250, 27.5) * mm, "end": v(250, 47.5) * mm});
            skLineSegment(sketch, "E120.0.2.0", {"start": v(250, 47.5) * mm, "end": v(260, 47.5) * mm});
            skLineSegment(sketch, "E120.direction1", {"start": v(250, -32.5) * mm, "end": v(275, -32.5) * mm, "construction": true});
            skLineSegment(sketch, "E120.direction2", {"start": v(250, -32.5) * mm, "end": v(250, 7.5) * mm, "construction": true});
            skLineSegment(sketch, "E121", {"start": v(255, -22.5) * mm, "end": v(250, -22.5) * mm, "construction": true});
            skLineSegment(sketch, "E122.MirrorCS", {"start": v(250, -32.5) * mm, "end": v(250, -52.5) * mm});
            skLineSegment(sketch, "E123.MirrorCS", {"start": v(250, -52.5) * mm, "end": v(260, -52.5) * mm});
            skLineSegment(sketch, "E124.MirrorCS", {"start": v(260, -72.5) * mm, "end": v(260, -52.5) * mm});
            skLineSegment(sketch, "E125.MirrorCS", {"start": v(250, -72.5) * mm, "end": v(260, -72.5) * mm});
            skLineSegment(sketch, "E126.MirrorCS", {"start": v(250, -72.5) * mm, "end": v(250, -92.5) * mm});
            skLineSegment(sketch, "E127.MirrorCS", {"start": v(250, -92.5) * mm, "end": v(260, -92.5) * mm});
            skLineSegment(sketch, "E128", {"start": v(235, -102.5) * mm, "end": v(260, -102.5) * mm});
            skLineSegment(sketch, "E129", {"start": v(260, -102.5) * mm, "end": v(260, -92.5) * mm});
            skLineSegment(sketch, "E130.MirrorCS", {"start": v(35, 47.5) * mm, "end": v(35, 57.5) * mm});
            skLineSegment(sketch, "E131.MirrorCS", {"start": v(115, 47.5) * mm, "end": v(115, 57.5) * mm});
            skLineSegment(sketch, "E132.MirrorCS", {"start": v(55, 47.5) * mm, "end": v(55, 57.5) * mm});
            skLineSegment(sketch, "E133.MirrorCS", {"start": v(155, 47.5) * mm, "end": v(155, 57.5) * mm});
            skLineSegment(sketch, "E134.MirrorCS", {"start": v(75, 47.5) * mm, "end": v(75, 57.5) * mm});
            skLineSegment(sketch, "E135.MirrorCS", {"start": v(235, 47.5) * mm, "end": v(235, 57.5) * mm});
            skLineSegment(sketch, "E136.MirrorCS", {"start": v(95, 47.5) * mm, "end": v(95, 57.5) * mm});
            skLineSegment(sketch, "E137.MirrorCS", {"start": v(15, 47.5) * mm, "end": v(15, 57.5) * mm});
            skLineSegment(sketch, "E138.MirrorCS", {"start": v(260, 57.5) * mm, "end": v(260, 47.5) * mm});
            skLineSegment(sketch, "E139.MirrorCS", {"start": v(175, 47.5) * mm, "end": v(175, 57.5) * mm});
            skLineSegment(sketch, "E140.MirrorCS", {"start": v(195, 47.5) * mm, "end": v(195, 57.5) * mm});
            skLineSegment(sketch, "E141.MirrorCS", {"start": v(135, 47.5) * mm, "end": v(135, 57.5) * mm});
            skLineSegment(sketch, "E142.MirrorCS", {"start": v(215, 47.5) * mm, "end": v(215, 57.5) * mm});
            skLineSegment(sketch, "E143.MirrorCS", {"start": v(135, 47.5) * mm, "end": v(155, 47.5) * mm});
            skLineSegment(sketch, "E144.MirrorCS", {"start": v(215, 47.5) * mm, "end": v(235, 47.5) * mm});
            skLineSegment(sketch, "E145.MirrorCS", {"start": v(175, 47.5) * mm, "end": v(195, 47.5) * mm});
            skLineSegment(sketch, "E146.MirrorCS", {"start": v(35, 47.5) * mm, "end": v(15, 47.5) * mm});
            skLineSegment(sketch, "E147.MirrorCS", {"start": v(115, 47.5) * mm, "end": v(95, 47.5) * mm});
            skLineSegment(sketch, "E148.MirrorCS", {"start": v(75, 47.5) * mm, "end": v(55, 47.5) * mm});
            skLineSegment(sketch, "E149.MirrorCS", {"start": v(135, 57.5) * mm, "end": v(115, 57.5) * mm});
            skLineSegment(sketch, "E150.MirrorCS", {"start": v(35, 57.5) * mm, "end": v(55, 57.5) * mm});
            skLineSegment(sketch, "E151.MirrorCS", {"start": v(175, 57.5) * mm, "end": v(155, 57.5) * mm});
            skLineSegment(sketch, "E152.MirrorCS", {"start": v(215, 57.5) * mm, "end": v(195, 57.5) * mm});
            skLineSegment(sketch, "E153.MirrorCS", {"start": v(75, 57.5) * mm, "end": v(95, 57.5) * mm});
            skLineSegment(sketch, "E154.MirrorCS", {"start": v(235, 57.5) * mm, "end": v(260, 57.5) * mm});
            skLineSegment(sketch, "E155.MirrorCS", {"start": v(15, -102.5) * mm, "end": v(-10, -102.5) * mm});
            skLineSegment(sketch, "E156.MirrorCS", {"start": v(-10, -102.5) * mm, "end": v(-10, -92.5) * mm});
            skLineSegment(sketch, "E157.MirrorCS", {"start": v(0, -92.5) * mm, "end": v(-10, -92.5) * mm});
            skLineSegment(sketch, "E158.MirrorCS", {"start": v(0, -72.5) * mm, "end": v(-10, -72.5) * mm});
            skLineSegment(sketch, "E159.MirrorCS", {"start": v(-10, -72.5) * mm, "end": v(-10, -52.5) * mm});
            skLineSegment(sketch, "E160.MirrorCS", {"start": v(0, -52.5) * mm, "end": v(-10, -52.5) * mm});
            skLineSegment(sketch, "E161.MirrorCS", {"start": v(0, -92.5) * mm, "end": v(0, 47.5) * mm, "construction": true});
            skLineSegment(sketch, "E162.MirrorCS", {"start": v(-10, -12.5) * mm, "end": v(-10, -32.5) * mm});
            skLineSegment(sketch, "E163.MirrorCS", {"start": v(0, -12.5) * mm, "end": v(-10, -12.5) * mm});
            skLineSegment(sketch, "E164.MirrorCS", {"start": v(0, 7.5) * mm, "end": v(-10, 7.5) * mm});
            skLineSegment(sketch, "E165.MirrorCS", {"start": v(-10, 27.5) * mm, "end": v(-10, 7.5) * mm});
            skLineSegment(sketch, "E166.MirrorCS", {"start": v(0, 27.5) * mm, "end": v(-10, 27.5) * mm});
            skLineSegment(sketch, "E167.MirrorCS", {"start": v(0, 47.5) * mm, "end": v(-10, 47.5) * mm});
            skLineSegment(sketch, "E168.MirrorCS", {"start": v(-10, 57.5) * mm, "end": v(-10, 47.5) * mm});
            skLineSegment(sketch, "E169.MirrorCS", {"start": v(0, 27.5) * mm, "end": v(0, 47.5) * mm});
            skLineSegment(sketch, "E170.MirrorCS", {"start": v(0, -12.5) * mm, "end": v(0, 7.5) * mm});
            skLineSegment(sketch, "E171.MirrorCS", {"start": v(0, -32.5) * mm, "end": v(0, -52.5) * mm});
            skLineSegment(sketch, "E172.MirrorCS", {"start": v(0, -72.5) * mm, "end": v(0, -92.5) * mm});
            skLineSegment(sketch, "E173.MirrorCS", {"start": v(0, -32.5) * mm, "end": v(-10, -32.5) * mm});
            skLineSegment(sketch, "E174", {"start": v(-10, 57.5) * mm, "end": v(15, 57.5) * mm});
            skSolve(sketch);
        }
        {
            var Q0;
            Q0=makeQuery(id+"F0.imprint","IMPRINT",FACE,{"disambiguationData":[TD([[makeQuery(id+"F0.imprint","IMPRINT",EDGE,{"derivedFrom":sQuery(id+"F0.wireOp",EDGE,"E7.bottom")}),1.0]])]});
            var Q1;
            Q1=makeQuery(id+"F0.imprint","IMPRINT",FACE,{"disambiguationData":[TD([[makeQuery(id+"F0.imprint","IMPRINT",EDGE,{"derivedFrom":sQuery(id+"F0.wireOp",EDGE,"E38.bottom")}),1.0]])]});
            var Q2;
            Q2=makeQuery(id+"F0.imprint","IMPRINT",FACE,{"disambiguationData":[TD([[makeQuery(id+"F0.imprint","IMPRINT",EDGE,{"derivedFrom":sQuery(id+"F0.wireOp",EDGE,"E24.bottom")}),1.0]])]});
            var Q3;
            Q3=makeQuery(id+"F0.imprint","IMPRINT",FACE,{"disambiguationData":[TD([[makeQuery(id+"F0.imprint","IMPRINT",EDGE,{"derivedFrom":sQuery(id+"F0.wireOp",EDGE,"E35.1.0.0")}),-1.0]])]});
            var Q4;
            Q4=makeQuery(id+"F0.imprint","IMPRINT",FACE,{"disambiguationData":[TD([[makeQuery(id+"F0.imprint","IMPRINT",EDGE,{"derivedFrom":sQuery(id+"F0.wireOp",EDGE,"E19.3.0.4")}),-1.0]])]});
            var Q5;
            Q5=makeQuery(id+"F0.imprint","IMPRINT",FACE,{"disambiguationData":[TD([[makeQuery(id+"F0.imprint","IMPRINT",EDGE,{"derivedFrom":sQuery(id+"F0.wireOp",EDGE,"E19.2.0.4")}),-1.0]])]});
            var Q6;
            Q6=makeQuery(id+"F0.imprint","IMPRINT",FACE,{"disambiguationData":[TD([[makeQuery(id+"F0.imprint","IMPRINT",EDGE,{"derivedFrom":sQuery(id+"F0.wireOp",EDGE,"E19.1.0.4")}),-1.0]])]});
            var Q7;
            Q7=makeQuery(id+"F0.imprint","IMPRINT",FACE,{"disambiguationData":[TD([[makeQuery(id+"F0.imprint","IMPRINT",EDGE,{"derivedFrom":sQuery(id+"F0.wireOp",EDGE,"E1")}),-1.0]])]});
            extrude(context, id + "F1", {"entities" : qUnion([Q0, Q1, Q2, Q3, Q4, Q5, Q6, Q7]), "oppositeDirection" : true, "depth" : 10 * mm});
        }
        {
            var Q0;
            Q0=makeQuery(id+"F0.imprint","IMPRINT",FACE,{"disambiguationData":[TD([[makeQuery(id+"F0.imprint","IMPRINT",EDGE,{"derivedFrom":sQuery(id+"F0.wireOp",EDGE,"E38.bottom")}),1.0]])]});
            var Q1;
            Q1=makeQuery(id+"F0.imprint","IMPRINT",FACE,{"disambiguationData":[TD([[makeQuery(id+"F0.imprint","IMPRINT",EDGE,{"derivedFrom":sQuery(id+"F0.wireOp",EDGE,"E1")}),-1.0]])]});
            var Q2;
            Q2=makeQuery(id+"F0.imprint","IMPRINT",FACE,{"disambiguationData":[TD([[makeQuery(id+"F0.imprint","IMPRINT",EDGE,{"derivedFrom":sQuery(id+"F0.wireOp",EDGE,"E19.1.0.4")}),-1.0]])]});
            var Q3;
            Q3=makeQuery(id+"F0.imprint","IMPRINT",FACE,{"disambiguationData":[TD([[makeQuery(id+"F0.imprint","IMPRINT",EDGE,{"derivedFrom":sQuery(id+"F0.wireOp",EDGE,"E19.2.0.4")}),-1.0]])]});
            var Q4;
            Q4=makeQuery(id+"F0.imprint","IMPRINT",FACE,{"disambiguationData":[TD([[makeQuery(id+"F0.imprint","IMPRINT",EDGE,{"derivedFrom":sQuery(id+"F0.wireOp",EDGE,"E19.3.0.4")}),-1.0]])]});
            var Q5;
            Q5=makeQuery(id+"F0.imprint","IMPRINT",FACE,{"disambiguationData":[TD([[makeQuery(id+"F0.imprint","IMPRINT",EDGE,{"derivedFrom":sQuery(id+"F0.wireOp",EDGE,"E35.1.0.0")}),-1.0]])]});
            var Q6;
            Q6=makeQuery(id+"F0.imprint","IMPRINT",FACE,{"disambiguationData":[TD([[makeQuery(id+"F0.imprint","IMPRINT",EDGE,{"derivedFrom":sQuery(id+"F0.wireOp",EDGE,"E24.bottom")}),1.0]])]});
            extrude(context, id + "F2", {"entities" : qUnion([Q0, Q1, Q2, Q3, Q4, Q5, Q6]), "operationType" : NewBodyOperationType.REMOVE, "oppositeDirection" : true, "depth" : 1 * mm});
        }
    });
